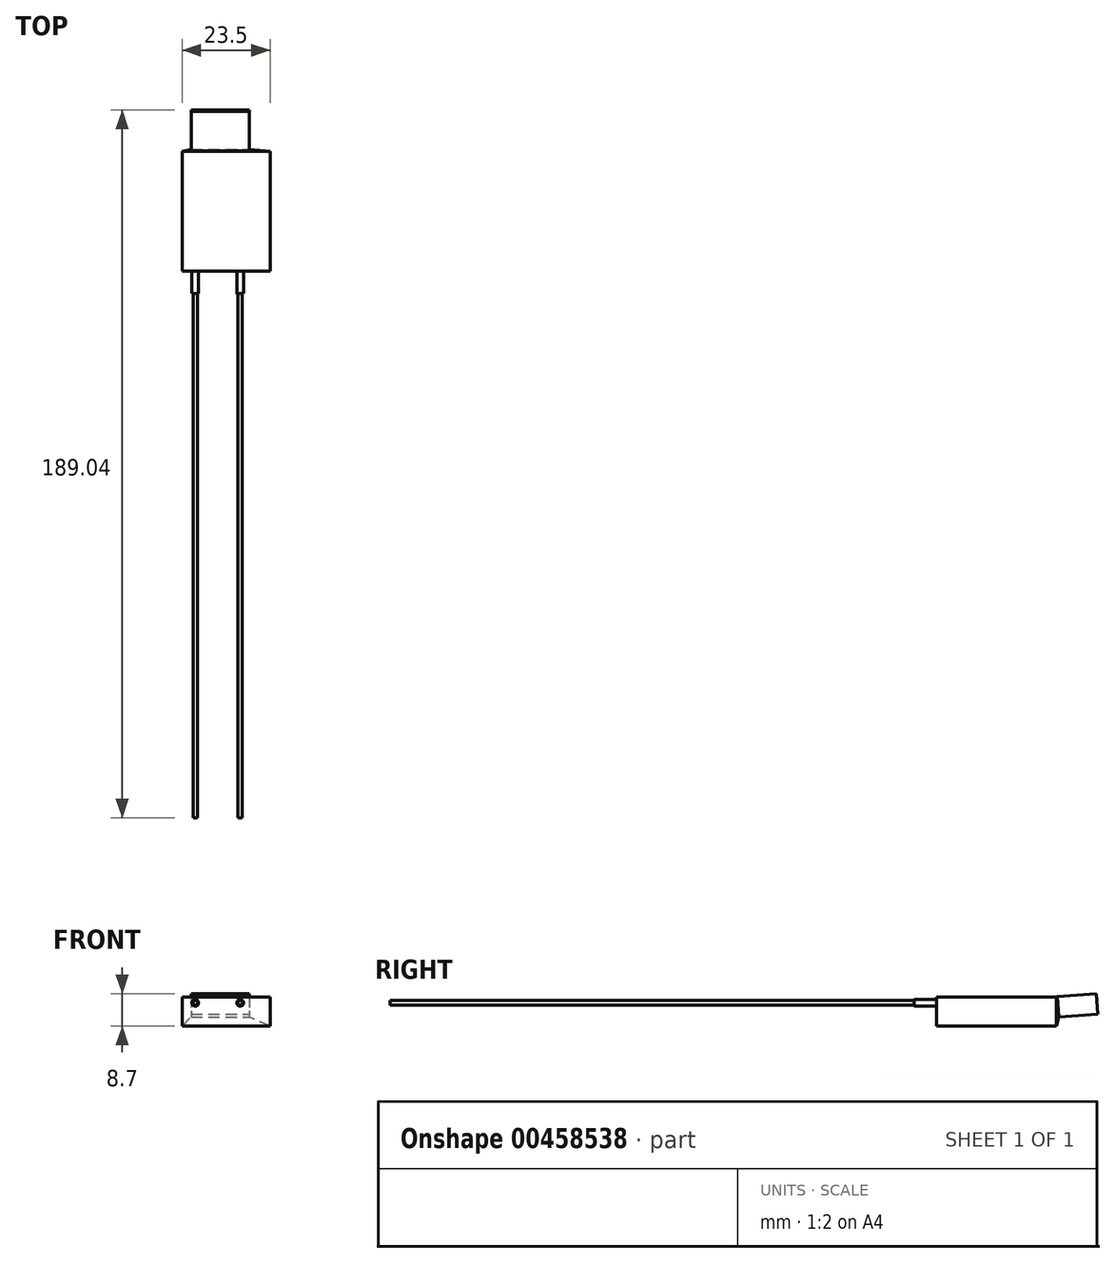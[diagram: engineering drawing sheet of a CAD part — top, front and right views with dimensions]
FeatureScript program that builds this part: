
annotation { "Feature Type Name" : "Feature", "Feature Type Description" : "" }
export const myFeature = defineFeature(function(context is Context, id is Id, definition is map)
    precondition{}
    {
        {
            var Q0;
            Q0=qCreatedBy(makeId("Top.planeOp"),FACE);
            var sketch = newSketch(context, id + "F0", { "sketchPlane" : qUnion([Q0])});
            skLineSegment(sketch, "E0.bottom", {"start": v(-11.75, 16) * mm, "end": v(11.75, 16) * mm});
            skLineSegment(sketch, "E0.top", {"start": v(-11.75, -16) * mm, "end": v(11.75, -16) * mm});
            skLineSegment(sketch, "E0.left", {"start": v(-11.75, 16) * mm, "end": v(-11.75, -16) * mm});
            skLineSegment(sketch, "E0.right", {"start": v(11.75, 16) * mm, "end": v(11.75, -16) * mm});
            skPoint(sketch, "E0.middle", {"position": v(0, 0) * mm});
            skSolve(sketch);
        }
        {
            var Q0;
            Q0=qSketchRegion(id+"F0",true);
            extrude(context, id + "F1", {"entities" : qUnion([Q0]), "depth" : 7.75 * mm});
        }
        {
            var Q0;
            Q0=makeQuery(id+"F1.opExtrude","CAP_EDGE",EDGE,{"disambiguationData":[OSD([sQuery(id+"F0.wireOp",EDGE,"E0.bottom")])],"isStart":false});
            cPlane(context, id + "F2", {"entities" : qUnion([Q0]), "cplaneType" : CPlaneType.LINE_ANGLE, "offset" : 25 * mm, "angle" : 4 * degree, "width" : 150 * mm, "height" : 150 * mm});
        }
        {
            var Q0;
            Q0=qCreatedBy(id+"F2.planeOp",FACE);
            cPlane(context, id + "F3", {"entities" : qUnion([Q0]), "cplaneType" : CPlaneType.OFFSET, "offset" : 0.2 * mm, "width" : 150 * mm, "height" : 150 * mm});
        }
        {
            var Q0;
            Q0=qCreatedBy(id+"F3.planeOp",FACE);
            var sketch = newSketch(context, id + "F4", { "sketchPlane" : qUnion([Q0])});
            skLineSegment(sketch, "E1.bottom", {"start": v(9.35, 6.82) * mm, "end": v(-6.15, 6.82) * mm});
            skLineSegment(sketch, "E1.top", {"start": v(9.35, 1.32) * mm, "end": v(-6.15, 1.32) * mm});
            skLineSegment(sketch, "E1.left", {"start": v(9.35, 6.82) * mm, "end": v(9.35, 1.32) * mm});
            skLineSegment(sketch, "E1.right", {"start": v(-6.15, 6.82) * mm, "end": v(-6.15, 1.32) * mm});
            skSolve(sketch);
        }
        {
            var Q0;
            Q0=qSketchRegion(id+"F4",true);
            extrude(context, id + "F5", {"entities" : qUnion([Q0]), "depth" : 10.5 * mm});
        }
        {
            var Q2;
            Q2=makeQuery(id+"F1.opExtrude","SWEPT_FACE",FACE,{"disambiguationData":[OSD([sQuery(id+"F0.wireOp",EDGE,"E0.bottom")])]});
            var Q3;
            Q3=makeQuery(id+"F5.opExtrude","CAP_FACE",FACE,{"disambiguationData":[OSD([sQuery(id+"F4.wireOp",EDGE,"E1.bottom"),sQuery(id+"F4.wireOp",EDGE,"E1.top"),sQuery(id+"F4.wireOp",EDGE,"E1.left"),sQuery(id+"F4.wireOp",EDGE,"E1.right")])],"isStart":true});
            loft(context, id + "F6", {"operationType" : NewBodyOperationType.ADD, "sheetProfilesArray" : [{ "sheetProfileEntities" : qUnion([Q2]) }, { "sheetProfileEntities" : qUnion([Q3]) }]});
        }
        {
            var Q0;
            Q0=makeQuery(id+"F1.opExtrude","SWEPT_FACE",FACE,{"disambiguationData":[OSD([sQuery(id+"F0.wireOp",EDGE,"E0.top")])]});
            var sketch = newSketch(context, id + "F7", { "sketchPlane" : qUnion([Q0])});
            skCircle(sketch, "E2", {"center": v(-8.25, 6.25) * mm, "radius": 0.9 * mm});
            skCircle(sketch, "E3", {"center": v(3.75, 6.25) * mm, "radius": 0.9 * mm});
            skSolve(sketch);
        }
        {
            var Q0;
            Q0=qSketchRegion(id+"F7",true);
            extrude(context, id + "F8", {"entities" : qUnion([Q0]), "operationType" : NewBodyOperationType.ADD, "depth" : 6 * mm});
        }
        {
            var Q0;
            Q0=makeQuery(id+"F8.opExtrude","CAP_FACE",FACE,{"disambiguationData":[OSD([sQuery(id+"F7.wireOp",EDGE,"E2")])],"isStart":false});
            var sketch = newSketch(context, id + "F9", { "sketchPlane" : qUnion([Q0])});
            skCircle(sketch, "E4", {"center": v(-8.25, 6.25) * mm, "radius": 0.6 * mm});
            skCircle(sketch, "E5", {"center": v(3.75, 6.25) * mm, "radius": 0.6 * mm});
            skSolve(sketch);
        }
        {
            var Q0;
            Q0=qSketchRegion(id+"F9",true);
            extrude(context, id + "F10", {"entities" : qUnion([Q0]), "operationType" : NewBodyOperationType.ADD, "depth" : 140 * mm});
        }
    });
